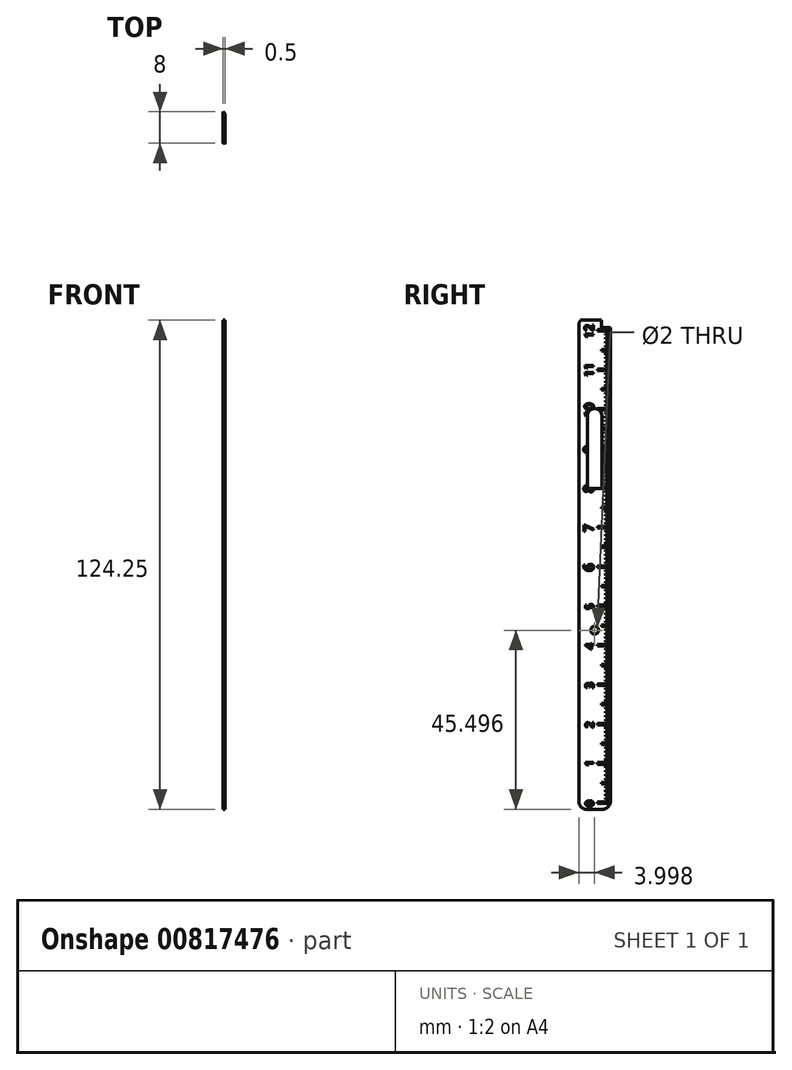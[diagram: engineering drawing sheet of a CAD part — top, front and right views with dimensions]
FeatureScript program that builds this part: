
annotation { "Feature Type Name" : "Feature", "Feature Type Description" : "" }
export const myFeature = defineFeature(function(context is Context, id is Id, definition is map)
    precondition{}
    {
        {
            var Q0;
            Q0=qCreatedBy(makeId("Right.planeOp"),FACE);
            var sketch = newSketch(context, id + "F0", { "sketchPlane" : qUnion([Q0])});
            skLineSegment(sketch, "E0.bottom", {"start": v(-20, 0) * mm, "end": v(-10, 0) * mm});
            skLineSegment(sketch, "E0.top", {"start": v(-20, 160) * mm, "end": v(-10, 160) * mm});
            skLineSegment(sketch, "E0.left", {"start": v(-20, 0) * mm, "end": v(-20, 160) * mm});
            skLineSegment(sketch, "E0.right", {"start": v(-10, 0) * mm, "end": v(-10, 160) * mm});
            skSolve(sketch);
        }
        {
            var Q0;
            Q0=qSketchRegion(id+"F0",true);
            extrude(context, id + "F1", {"entities" : qUnion([Q0]), "depth" : 1 * mm, "offsetDistance" : 25 * mm});
        }
        {
            var Q0;
            Q0=qCreatedBy(makeId("Right.planeOp"),FACE);
            var sketch = newSketch(context, id + "F2", { "sketchPlane" : qUnion([Q0])});
            skLineSegment(sketch, "E1", {"start": v(-12, 0) * mm, "end": v(-12, 150) * mm, "construction": true});
            skLineSegment(sketch, "E2", {"start": v(-14, 0) * mm, "end": v(-14, 150) * mm, "construction": true});
            skLineSegment(sketch, "E3", {"start": v(-13, 0) * mm, "end": v(-13, 150) * mm, "construction": true});
            skLineSegment(sketch, "E4.bottom", {"start": v(-14, 10.4) * mm, "end": v(-10, 10.4) * mm});
            skLineSegment(sketch, "E4.top", {"start": v(-14, 10) * mm, "end": v(-10, 10) * mm});
            skLineSegment(sketch, "E4.left", {"start": v(-14, 10) * mm, "end": v(-14, 10.4) * mm});
            skLineSegment(sketch, "E4.right", {"start": v(-10, 10) * mm, "end": v(-10, 10.4) * mm});
            skLineSegment(sketch, "E5.0.1.0", {"start": v(-14, 20.4) * mm, "end": v(-10, 20.4) * mm});
            skLineSegment(sketch, "E5.0.1.1", {"start": v(-14, 20) * mm, "end": v(-10, 20) * mm});
            skLineSegment(sketch, "E5.0.1.2", {"start": v(-14, 20) * mm, "end": v(-14, 20.4) * mm});
            skLineSegment(sketch, "E5.0.1.3", {"start": v(-10, 20) * mm, "end": v(-10, 20.4) * mm});
            skLineSegment(sketch, "E5.0.2.0", {"start": v(-14, 30.4) * mm, "end": v(-10, 30.4) * mm});
            skLineSegment(sketch, "E5.0.2.1", {"start": v(-14, 30) * mm, "end": v(-10, 30) * mm});
            skLineSegment(sketch, "E5.0.2.2", {"start": v(-14, 30) * mm, "end": v(-14, 30.4) * mm});
            skLineSegment(sketch, "E5.0.2.3", {"start": v(-10, 30) * mm, "end": v(-10, 30.4) * mm});
            skLineSegment(sketch, "E5.0.3.0", {"start": v(-14, 40.4) * mm, "end": v(-10, 40.4) * mm});
            skLineSegment(sketch, "E5.0.3.1", {"start": v(-14, 40) * mm, "end": v(-10, 40) * mm});
            skLineSegment(sketch, "E5.0.3.2", {"start": v(-14, 40) * mm, "end": v(-14, 40.4) * mm});
            skLineSegment(sketch, "E5.0.3.3", {"start": v(-10, 40) * mm, "end": v(-10, 40.4) * mm});
            skLineSegment(sketch, "E5.0.4.0", {"start": v(-14, 50.4) * mm, "end": v(-10, 50.4) * mm});
            skLineSegment(sketch, "E5.0.4.1", {"start": v(-14, 50) * mm, "end": v(-10, 50) * mm});
            skLineSegment(sketch, "E5.0.4.2", {"start": v(-14, 50) * mm, "end": v(-14, 50.4) * mm});
            skLineSegment(sketch, "E5.0.4.3", {"start": v(-10, 50) * mm, "end": v(-10, 50.4) * mm});
            skLineSegment(sketch, "E5.0.5.0", {"start": v(-14, 60.4) * mm, "end": v(-10, 60.4) * mm});
            skLineSegment(sketch, "E5.0.5.1", {"start": v(-14, 60) * mm, "end": v(-10, 60) * mm});
            skLineSegment(sketch, "E5.0.5.2", {"start": v(-14, 60) * mm, "end": v(-14, 60.4) * mm});
            skLineSegment(sketch, "E5.0.5.3", {"start": v(-10, 60) * mm, "end": v(-10, 60.4) * mm});
            skLineSegment(sketch, "E5.0.6.0", {"start": v(-14, 70.4) * mm, "end": v(-10, 70.4) * mm});
            skLineSegment(sketch, "E5.0.6.1", {"start": v(-14, 70) * mm, "end": v(-10, 70) * mm});
            skLineSegment(sketch, "E5.0.6.2", {"start": v(-14, 70) * mm, "end": v(-14, 70.4) * mm});
            skLineSegment(sketch, "E5.0.6.3", {"start": v(-10, 70) * mm, "end": v(-10, 70.4) * mm});
            skLineSegment(sketch, "E5.0.7.0", {"start": v(-14, 80.4) * mm, "end": v(-10, 80.4) * mm});
            skLineSegment(sketch, "E5.0.7.1", {"start": v(-14, 80) * mm, "end": v(-10, 80) * mm});
            skLineSegment(sketch, "E5.0.7.2", {"start": v(-14, 80) * mm, "end": v(-14, 80.4) * mm});
            skLineSegment(sketch, "E5.0.7.3", {"start": v(-10, 80) * mm, "end": v(-10, 80.4) * mm});
            skLineSegment(sketch, "E5.0.8.0", {"start": v(-14, 90.4) * mm, "end": v(-10, 90.4) * mm});
            skLineSegment(sketch, "E5.0.8.1", {"start": v(-14, 90) * mm, "end": v(-10, 90) * mm});
            skLineSegment(sketch, "E5.0.8.2", {"start": v(-14, 90) * mm, "end": v(-14, 90.4) * mm});
            skLineSegment(sketch, "E5.0.8.3", {"start": v(-10, 90) * mm, "end": v(-10, 90.4) * mm});
            skLineSegment(sketch, "E5.0.9.0", {"start": v(-14, 100.4) * mm, "end": v(-10, 100.4) * mm});
            skLineSegment(sketch, "E5.0.9.1", {"start": v(-14, 100) * mm, "end": v(-10, 100) * mm});
            skLineSegment(sketch, "E5.0.9.2", {"start": v(-14, 100) * mm, "end": v(-14, 100.4) * mm});
            skLineSegment(sketch, "E5.0.9.3", {"start": v(-10, 100) * mm, "end": v(-10, 100.4) * mm});
            skLineSegment(sketch, "E5.direction2", {"start": v(-14, 10) * mm, "end": v(-14, 20) * mm, "construction": true});
            skLineSegment(sketch, "E6.0.0.10", {"start": v(-14, 110.4) * mm, "end": v(-10, 110.4) * mm});
            skLineSegment(sketch, "E6.3.0.10", {"start": v(-14, 110) * mm, "end": v(-10, 110) * mm});
            skLineSegment(sketch, "E6.6.0.10", {"start": v(-14, 110) * mm, "end": v(-14, 110.4) * mm});
            skLineSegment(sketch, "E6.9.0.10", {"start": v(-10, 110) * mm, "end": v(-10, 110.4) * mm});
            skLineSegment(sketch, "E6.0.0.11", {"start": v(-14, 120.4) * mm, "end": v(-10, 120.4) * mm});
            skLineSegment(sketch, "E6.3.0.11", {"start": v(-14, 120) * mm, "end": v(-10, 120) * mm});
            skLineSegment(sketch, "E6.6.0.11", {"start": v(-14, 120) * mm, "end": v(-14, 120.4) * mm});
            skLineSegment(sketch, "E6.9.0.11", {"start": v(-10, 120) * mm, "end": v(-10, 120.4) * mm});
            skLineSegment(sketch, "E6.0.0.12", {"start": v(-14, 130.4) * mm, "end": v(-10, 130.4) * mm});
            skLineSegment(sketch, "E6.3.0.12", {"start": v(-14, 130) * mm, "end": v(-10, 130) * mm});
            skLineSegment(sketch, "E6.6.0.12", {"start": v(-14, 130) * mm, "end": v(-14, 130.4) * mm});
            skLineSegment(sketch, "E6.9.0.12", {"start": v(-10, 130) * mm, "end": v(-10, 130.4) * mm});
            skLineSegment(sketch, "E6.0.0.13", {"start": v(-14, 140.4) * mm, "end": v(-10, 140.4) * mm});
            skLineSegment(sketch, "E6.3.0.13", {"start": v(-14, 140) * mm, "end": v(-10, 140) * mm});
            skLineSegment(sketch, "E6.6.0.13", {"start": v(-14, 140) * mm, "end": v(-14, 140.4) * mm});
            skLineSegment(sketch, "E6.9.0.13", {"start": v(-10, 140) * mm, "end": v(-10, 140.4) * mm});
            skLineSegment(sketch, "E7.bottom", {"start": v(-10, 15) * mm, "end": v(-13, 15) * mm});
            skLineSegment(sketch, "E7.top", {"start": v(-10, 15.4) * mm, "end": v(-13, 15.4) * mm});
            skLineSegment(sketch, "E7.left", {"start": v(-10, 15) * mm, "end": v(-10, 15.4) * mm});
            skLineSegment(sketch, "E7.right", {"start": v(-13, 15) * mm, "end": v(-13, 15.4) * mm});
            skLineSegment(sketch, "E8", {"start": v(-22.56, 0) * mm, "end": v(-10, 0) * mm, "construction": true});
            skLineSegment(sketch, "E9", {"start": v(-15, 150) * mm, "end": v(-15, 0) * mm, "construction": true});
            skText(sketch, "E10", { "text": "0", "fontName": "OpenSans-Regular.ttf"});
            skText(sketch, "E11", { "text": "1\n", "fontName": "OpenSans-Regular.ttf"});
            skText(sketch, "E12", { "text": "2", "fontName": "OpenSans-Regular.ttf"});
            skText(sketch, "E13", { "text": "3", "fontName": "OpenSans-Regular.ttf"});
            skText(sketch, "E14", { "text": "4", "fontName": "OpenSans-Regular.ttf"});
            skText(sketch, "E15", { "text": "5", "fontName": "OpenSans-Regular.ttf"});
            skText(sketch, "E16", { "text": "6", "fontName": "OpenSans-Regular.ttf"});
            skText(sketch, "E17", { "text": "7", "fontName": "OpenSans-Regular.ttf"});
            skText(sketch, "E18", { "text": "8", "fontName": "OpenSans-Regular.ttf"});
            skText(sketch, "E19", { "text": "9", "fontName": "OpenSans-Regular.ttf"});
            skText(sketch, "E20", { "text": "10", "fontName": "OpenSans-Regular.ttf"});
            skText(sketch, "E21", { "text": "11", "fontName": "OpenSans-Regular.ttf"});
            skText(sketch, "E22", { "text": "12", "fontName": "OpenSans-Regular.ttf"});
            skText(sketch, "E23", { "text": "13", "fontName": "OpenSans-Regular.ttf"});
            skLineSegment(sketch, "E24.bottom", {"start": v(-12, 11) * mm, "end": v(-10, 11) * mm});
            skLineSegment(sketch, "E24.top", {"start": v(-12, 11.4) * mm, "end": v(-10, 11.4) * mm});
            skLineSegment(sketch, "E24.left", {"start": v(-12, 11) * mm, "end": v(-12, 11.4) * mm});
            skLineSegment(sketch, "E24.right", {"start": v(-10, 11) * mm, "end": v(-10, 11.4) * mm});
            skLineSegment(sketch, "E25.bottom", {"start": v(-12, 12) * mm, "end": v(-10, 12) * mm});
            skLineSegment(sketch, "E25.top", {"start": v(-12, 12.4) * mm, "end": v(-10, 12.4) * mm});
            skLineSegment(sketch, "E25.left", {"start": v(-12, 12) * mm, "end": v(-12, 12.4) * mm});
            skLineSegment(sketch, "E25.right", {"start": v(-10, 12) * mm, "end": v(-10, 12.4) * mm});
            skLineSegment(sketch, "E26.bottom", {"start": v(-12, 13) * mm, "end": v(-10, 13) * mm});
            skLineSegment(sketch, "E26.top", {"start": v(-12, 13.4) * mm, "end": v(-10, 13.4) * mm});
            skLineSegment(sketch, "E26.left", {"start": v(-12, 13) * mm, "end": v(-12, 13.4) * mm});
            skLineSegment(sketch, "E26.right", {"start": v(-10, 13) * mm, "end": v(-10, 13.4) * mm});
            skLineSegment(sketch, "E27.bottom", {"start": v(-12, 14) * mm, "end": v(-10, 14) * mm});
            skLineSegment(sketch, "E27.top", {"start": v(-12, 14.4) * mm, "end": v(-10, 14.4) * mm});
            skLineSegment(sketch, "E27.left", {"start": v(-12, 14) * mm, "end": v(-12, 14.4) * mm});
            skLineSegment(sketch, "E27.right", {"start": v(-10, 14) * mm, "end": v(-10, 14.4) * mm});
            skLineSegment(sketch, "E28.bottom", {"start": v(-12, 16) * mm, "end": v(-10, 16) * mm});
            skLineSegment(sketch, "E28.top", {"start": v(-12, 16.4) * mm, "end": v(-10, 16.4) * mm});
            skLineSegment(sketch, "E28.left", {"start": v(-12, 16) * mm, "end": v(-12, 16.4) * mm});
            skLineSegment(sketch, "E28.right", {"start": v(-10, 16) * mm, "end": v(-10, 16.4) * mm});
            skLineSegment(sketch, "E29.bottom", {"start": v(-12, 17) * mm, "end": v(-10, 17) * mm});
            skLineSegment(sketch, "E29.top", {"start": v(-12, 17.4) * mm, "end": v(-10, 17.4) * mm});
            skLineSegment(sketch, "E29.left", {"start": v(-12, 17) * mm, "end": v(-12, 17.4) * mm});
            skLineSegment(sketch, "E29.right", {"start": v(-10, 17) * mm, "end": v(-10, 17.4) * mm});
            skLineSegment(sketch, "E30.bottom", {"start": v(-12, 18) * mm, "end": v(-10, 18) * mm});
            skLineSegment(sketch, "E30.top", {"start": v(-12, 18.4) * mm, "end": v(-10, 18.4) * mm});
            skLineSegment(sketch, "E30.left", {"start": v(-12, 18) * mm, "end": v(-12, 18.4) * mm});
            skLineSegment(sketch, "E30.right", {"start": v(-10, 18) * mm, "end": v(-10, 18.4) * mm});
            skLineSegment(sketch, "E31.bottom", {"start": v(-12, 19) * mm, "end": v(-10, 19) * mm});
            skLineSegment(sketch, "E31.top", {"start": v(-12, 19.4) * mm, "end": v(-10, 19.4) * mm});
            skLineSegment(sketch, "E31.left", {"start": v(-12, 19) * mm, "end": v(-12, 19.4) * mm});
            skLineSegment(sketch, "E31.right", {"start": v(-10, 19) * mm, "end": v(-10, 19.4) * mm});
            skLineSegment(sketch, "E32.0.1.0", {"start": v(-12, 22) * mm, "end": v(-10, 22) * mm});
            skLineSegment(sketch, "E32.0.1.1", {"start": v(-12, 21.4) * mm, "end": v(-10, 21.4) * mm});
            skLineSegment(sketch, "E32.0.1.2", {"start": v(-12, 23.4) * mm, "end": v(-10, 23.4) * mm});
            skLineSegment(sketch, "E32.0.1.3", {"start": v(-12, 28.4) * mm, "end": v(-10, 28.4) * mm});
            skLineSegment(sketch, "E32.0.1.4", {"start": v(-12, 22.4) * mm, "end": v(-10, 22.4) * mm});
            skLineSegment(sketch, "E32.0.1.5", {"start": v(-12, 23) * mm, "end": v(-10, 23) * mm});
            skLineSegment(sketch, "E32.0.1.6", {"start": v(-10, 25.4) * mm, "end": v(-13, 25.4) * mm});
            skLineSegment(sketch, "E32.0.1.7", {"start": v(-12, 29) * mm, "end": v(-10, 29) * mm});
            skLineSegment(sketch, "E32.0.1.8", {"start": v(-12, 29.4) * mm, "end": v(-10, 29.4) * mm});
            skLineSegment(sketch, "E32.0.1.9", {"start": v(-12, 24.4) * mm, "end": v(-10, 24.4) * mm});
            skLineSegment(sketch, "E32.0.1.10", {"start": v(-12, 28) * mm, "end": v(-10, 28) * mm});
            skLineSegment(sketch, "E32.0.1.11", {"start": v(-12, 26) * mm, "end": v(-10, 26) * mm});
            skLineSegment(sketch, "E32.0.1.12", {"start": v(-12, 27) * mm, "end": v(-10, 27) * mm});
            skLineSegment(sketch, "E32.0.1.13", {"start": v(-12, 26.4) * mm, "end": v(-10, 26.4) * mm});
            skLineSegment(sketch, "E32.0.1.14", {"start": v(-12, 21) * mm, "end": v(-10, 21) * mm});
            skLineSegment(sketch, "E32.0.1.15", {"start": v(-10, 25) * mm, "end": v(-13, 25) * mm});
            skLineSegment(sketch, "E32.0.1.16", {"start": v(-12, 10) * mm, "end": v(-12, 160) * mm, "construction": true});
            skLineSegment(sketch, "E32.0.1.17", {"start": v(-13, 10) * mm, "end": v(-13, 160) * mm, "construction": true});
            skLineSegment(sketch, "E32.0.1.18", {"start": v(-12, 24) * mm, "end": v(-10, 24) * mm});
            skLineSegment(sketch, "E32.0.1.19", {"start": v(-12, 27.4) * mm, "end": v(-10, 27.4) * mm});
            skLineSegment(sketch, "E32.0.1.20", {"start": v(-12, 21) * mm, "end": v(-12, 21.4) * mm});
            skLineSegment(sketch, "E32.0.1.21", {"start": v(-10, 24) * mm, "end": v(-10, 24.4) * mm});
            skLineSegment(sketch, "E32.0.1.22", {"start": v(-10, 27) * mm, "end": v(-10, 27.4) * mm});
            skLineSegment(sketch, "E32.0.1.23", {"start": v(-12, 29) * mm, "end": v(-12, 29.4) * mm});
            skLineSegment(sketch, "E32.0.1.24", {"start": v(-10, 25) * mm, "end": v(-10, 25.4) * mm});
            skLineSegment(sketch, "E32.0.1.25", {"start": v(-12, 24) * mm, "end": v(-12, 24.4) * mm});
            skLineSegment(sketch, "E32.0.1.26", {"start": v(-12, 26) * mm, "end": v(-12, 26.4) * mm});
            skLineSegment(sketch, "E32.0.1.27", {"start": v(-10, 28) * mm, "end": v(-10, 28.4) * mm});
            skLineSegment(sketch, "E32.0.1.28", {"start": v(-12, 28) * mm, "end": v(-12, 28.4) * mm});
            skLineSegment(sketch, "E32.0.1.29", {"start": v(-10, 21) * mm, "end": v(-10, 21.4) * mm});
            skLineSegment(sketch, "E32.0.1.30", {"start": v(-10, 26) * mm, "end": v(-10, 26.4) * mm});
            skLineSegment(sketch, "E32.0.1.31", {"start": v(-10, 29) * mm, "end": v(-10, 29.4) * mm});
            skLineSegment(sketch, "E32.0.1.32", {"start": v(-12, 22) * mm, "end": v(-12, 22.4) * mm});
            skLineSegment(sketch, "E32.0.1.33", {"start": v(-10, 23) * mm, "end": v(-10, 23.4) * mm});
            skLineSegment(sketch, "E32.0.1.34", {"start": v(-13, 25) * mm, "end": v(-13, 25.4) * mm});
            skLineSegment(sketch, "E32.0.1.35", {"start": v(-10, 22) * mm, "end": v(-10, 22.4) * mm});
            skLineSegment(sketch, "E32.0.1.36", {"start": v(-12, 27) * mm, "end": v(-12, 27.4) * mm});
            skLineSegment(sketch, "E32.0.1.37", {"start": v(-12, 23) * mm, "end": v(-12, 23.4) * mm});
            skLineSegment(sketch, "E32.0.2.0", {"start": v(-12, 32) * mm, "end": v(-10, 32) * mm});
            skLineSegment(sketch, "E32.0.2.1", {"start": v(-12, 31.4) * mm, "end": v(-10, 31.4) * mm});
            skLineSegment(sketch, "E32.0.2.2", {"start": v(-12, 33.4) * mm, "end": v(-10, 33.4) * mm});
            skLineSegment(sketch, "E32.0.2.3", {"start": v(-12, 38.4) * mm, "end": v(-10, 38.4) * mm});
            skLineSegment(sketch, "E32.0.2.4", {"start": v(-12, 32.4) * mm, "end": v(-10, 32.4) * mm});
            skLineSegment(sketch, "E32.0.2.5", {"start": v(-12, 33) * mm, "end": v(-10, 33) * mm});
            skLineSegment(sketch, "E32.0.2.6", {"start": v(-10, 35.4) * mm, "end": v(-13, 35.4) * mm});
            skLineSegment(sketch, "E32.0.2.7", {"start": v(-12, 39) * mm, "end": v(-10, 39) * mm});
            skLineSegment(sketch, "E32.0.2.8", {"start": v(-12, 39.4) * mm, "end": v(-10, 39.4) * mm});
            skLineSegment(sketch, "E32.0.2.9", {"start": v(-12, 34.4) * mm, "end": v(-10, 34.4) * mm});
            skLineSegment(sketch, "E32.0.2.10", {"start": v(-12, 38) * mm, "end": v(-10, 38) * mm});
            skLineSegment(sketch, "E32.0.2.11", {"start": v(-12, 36) * mm, "end": v(-10, 36) * mm});
            skLineSegment(sketch, "E32.0.2.12", {"start": v(-12, 37) * mm, "end": v(-10, 37) * mm});
            skLineSegment(sketch, "E32.0.2.13", {"start": v(-12, 36.4) * mm, "end": v(-10, 36.4) * mm});
            skLineSegment(sketch, "E32.0.2.14", {"start": v(-12, 31) * mm, "end": v(-10, 31) * mm});
            skLineSegment(sketch, "E32.0.2.15", {"start": v(-10, 35) * mm, "end": v(-13, 35) * mm});
            skLineSegment(sketch, "E32.0.2.16", {"start": v(-12, 20) * mm, "end": v(-12, 170) * mm, "construction": true});
            skLineSegment(sketch, "E32.0.2.17", {"start": v(-13, 20) * mm, "end": v(-13, 170) * mm, "construction": true});
            skLineSegment(sketch, "E32.0.2.18", {"start": v(-12, 34) * mm, "end": v(-10, 34) * mm});
            skLineSegment(sketch, "E32.0.2.19", {"start": v(-12, 37.4) * mm, "end": v(-10, 37.4) * mm});
            skLineSegment(sketch, "E32.0.2.20", {"start": v(-12, 31) * mm, "end": v(-12, 31.4) * mm});
            skLineSegment(sketch, "E32.0.2.21", {"start": v(-10, 34) * mm, "end": v(-10, 34.4) * mm});
            skLineSegment(sketch, "E32.0.2.22", {"start": v(-10, 37) * mm, "end": v(-10, 37.4) * mm});
            skLineSegment(sketch, "E32.0.2.23", {"start": v(-12, 39) * mm, "end": v(-12, 39.4) * mm});
            skLineSegment(sketch, "E32.0.2.24", {"start": v(-10, 35) * mm, "end": v(-10, 35.4) * mm});
            skLineSegment(sketch, "E32.0.2.25", {"start": v(-12, 34) * mm, "end": v(-12, 34.4) * mm});
            skLineSegment(sketch, "E32.0.2.26", {"start": v(-12, 36) * mm, "end": v(-12, 36.4) * mm});
            skLineSegment(sketch, "E32.0.2.27", {"start": v(-10, 38) * mm, "end": v(-10, 38.4) * mm});
            skLineSegment(sketch, "E32.0.2.28", {"start": v(-12, 38) * mm, "end": v(-12, 38.4) * mm});
            skLineSegment(sketch, "E32.0.2.29", {"start": v(-10, 31) * mm, "end": v(-10, 31.4) * mm});
            skLineSegment(sketch, "E32.0.2.30", {"start": v(-10, 36) * mm, "end": v(-10, 36.4) * mm});
            skLineSegment(sketch, "E32.0.2.31", {"start": v(-10, 39) * mm, "end": v(-10, 39.4) * mm});
            skLineSegment(sketch, "E32.0.2.32", {"start": v(-12, 32) * mm, "end": v(-12, 32.4) * mm});
            skLineSegment(sketch, "E32.0.2.33", {"start": v(-10, 33) * mm, "end": v(-10, 33.4) * mm});
            skLineSegment(sketch, "E32.0.2.34", {"start": v(-13, 35) * mm, "end": v(-13, 35.4) * mm});
            skLineSegment(sketch, "E32.0.2.35", {"start": v(-10, 32) * mm, "end": v(-10, 32.4) * mm});
            skLineSegment(sketch, "E32.0.2.36", {"start": v(-12, 37) * mm, "end": v(-12, 37.4) * mm});
            skLineSegment(sketch, "E32.0.2.37", {"start": v(-12, 33) * mm, "end": v(-12, 33.4) * mm});
            skLineSegment(sketch, "E32.0.3.0", {"start": v(-12, 42) * mm, "end": v(-10, 42) * mm});
            skLineSegment(sketch, "E32.0.3.1", {"start": v(-12, 41.4) * mm, "end": v(-10, 41.4) * mm});
            skLineSegment(sketch, "E32.0.3.2", {"start": v(-12, 43.4) * mm, "end": v(-10, 43.4) * mm});
            skLineSegment(sketch, "E32.0.3.3", {"start": v(-12, 48.4) * mm, "end": v(-10, 48.4) * mm});
            skLineSegment(sketch, "E32.0.3.4", {"start": v(-12, 42.4) * mm, "end": v(-10, 42.4) * mm});
            skLineSegment(sketch, "E32.0.3.5", {"start": v(-12, 43) * mm, "end": v(-10, 43) * mm});
            skLineSegment(sketch, "E32.0.3.6", {"start": v(-10, 45.4) * mm, "end": v(-13, 45.4) * mm});
            skLineSegment(sketch, "E32.0.3.7", {"start": v(-12, 49) * mm, "end": v(-10, 49) * mm});
            skLineSegment(sketch, "E32.0.3.8", {"start": v(-12, 49.4) * mm, "end": v(-10, 49.4) * mm});
            skLineSegment(sketch, "E32.0.3.9", {"start": v(-12, 44.4) * mm, "end": v(-10, 44.4) * mm});
            skLineSegment(sketch, "E32.0.3.10", {"start": v(-12, 48) * mm, "end": v(-10, 48) * mm});
            skLineSegment(sketch, "E32.0.3.11", {"start": v(-12, 46) * mm, "end": v(-10, 46) * mm});
            skLineSegment(sketch, "E32.0.3.12", {"start": v(-12, 47) * mm, "end": v(-10, 47) * mm});
            skLineSegment(sketch, "E32.0.3.13", {"start": v(-12, 46.4) * mm, "end": v(-10, 46.4) * mm});
            skLineSegment(sketch, "E32.0.3.14", {"start": v(-12, 41) * mm, "end": v(-10, 41) * mm});
            skLineSegment(sketch, "E32.0.3.15", {"start": v(-10, 45) * mm, "end": v(-13, 45) * mm});
            skLineSegment(sketch, "E32.0.3.16", {"start": v(-12, 30) * mm, "end": v(-12, 180) * mm, "construction": true});
            skLineSegment(sketch, "E32.0.3.17", {"start": v(-13, 30) * mm, "end": v(-13, 180) * mm, "construction": true});
            skLineSegment(sketch, "E32.0.3.18", {"start": v(-12, 44) * mm, "end": v(-10, 44) * mm});
            skLineSegment(sketch, "E32.0.3.19", {"start": v(-12, 47.4) * mm, "end": v(-10, 47.4) * mm});
            skLineSegment(sketch, "E32.0.3.20", {"start": v(-12, 41) * mm, "end": v(-12, 41.4) * mm});
            skLineSegment(sketch, "E32.0.3.21", {"start": v(-10, 44) * mm, "end": v(-10, 44.4) * mm});
            skLineSegment(sketch, "E32.0.3.22", {"start": v(-10, 47) * mm, "end": v(-10, 47.4) * mm});
            skLineSegment(sketch, "E32.0.3.23", {"start": v(-12, 49) * mm, "end": v(-12, 49.4) * mm});
            skLineSegment(sketch, "E32.0.3.24", {"start": v(-10, 45) * mm, "end": v(-10, 45.4) * mm});
            skLineSegment(sketch, "E32.0.3.25", {"start": v(-12, 44) * mm, "end": v(-12, 44.4) * mm});
            skLineSegment(sketch, "E32.0.3.26", {"start": v(-12, 46) * mm, "end": v(-12, 46.4) * mm});
            skLineSegment(sketch, "E32.0.3.27", {"start": v(-10, 48) * mm, "end": v(-10, 48.4) * mm});
            skLineSegment(sketch, "E32.0.3.28", {"start": v(-12, 48) * mm, "end": v(-12, 48.4) * mm});
            skLineSegment(sketch, "E32.0.3.29", {"start": v(-10, 41) * mm, "end": v(-10, 41.4) * mm});
            skLineSegment(sketch, "E32.0.3.30", {"start": v(-10, 46) * mm, "end": v(-10, 46.4) * mm});
            skLineSegment(sketch, "E32.0.3.31", {"start": v(-10, 49) * mm, "end": v(-10, 49.4) * mm});
            skLineSegment(sketch, "E32.0.3.32", {"start": v(-12, 42) * mm, "end": v(-12, 42.4) * mm});
            skLineSegment(sketch, "E32.0.3.33", {"start": v(-10, 43) * mm, "end": v(-10, 43.4) * mm});
            skLineSegment(sketch, "E32.0.3.34", {"start": v(-13, 45) * mm, "end": v(-13, 45.4) * mm});
            skLineSegment(sketch, "E32.0.3.35", {"start": v(-10, 42) * mm, "end": v(-10, 42.4) * mm});
            skLineSegment(sketch, "E32.0.3.36", {"start": v(-12, 47) * mm, "end": v(-12, 47.4) * mm});
            skLineSegment(sketch, "E32.0.3.37", {"start": v(-12, 43) * mm, "end": v(-12, 43.4) * mm});
            skLineSegment(sketch, "E32.0.4.0", {"start": v(-12, 52) * mm, "end": v(-10, 52) * mm});
            skLineSegment(sketch, "E32.0.4.1", {"start": v(-12, 51.4) * mm, "end": v(-10, 51.4) * mm});
            skLineSegment(sketch, "E32.0.4.2", {"start": v(-12, 53.4) * mm, "end": v(-10, 53.4) * mm});
            skLineSegment(sketch, "E32.0.4.3", {"start": v(-12, 58.4) * mm, "end": v(-10, 58.4) * mm});
            skLineSegment(sketch, "E32.0.4.4", {"start": v(-12, 52.4) * mm, "end": v(-10, 52.4) * mm});
            skLineSegment(sketch, "E32.0.4.5", {"start": v(-12, 53) * mm, "end": v(-10, 53) * mm});
            skLineSegment(sketch, "E32.0.4.6", {"start": v(-10, 55.4) * mm, "end": v(-13, 55.4) * mm});
            skLineSegment(sketch, "E32.0.4.7", {"start": v(-12, 59) * mm, "end": v(-10, 59) * mm});
            skLineSegment(sketch, "E32.0.4.8", {"start": v(-12, 59.4) * mm, "end": v(-10, 59.4) * mm});
            skLineSegment(sketch, "E32.0.4.9", {"start": v(-12, 54.4) * mm, "end": v(-10, 54.4) * mm});
            skLineSegment(sketch, "E32.0.4.10", {"start": v(-12, 58) * mm, "end": v(-10, 58) * mm});
            skLineSegment(sketch, "E32.0.4.11", {"start": v(-12, 56) * mm, "end": v(-10, 56) * mm});
            skLineSegment(sketch, "E32.0.4.12", {"start": v(-12, 57) * mm, "end": v(-10, 57) * mm});
            skLineSegment(sketch, "E32.0.4.13", {"start": v(-12, 56.4) * mm, "end": v(-10, 56.4) * mm});
            skLineSegment(sketch, "E32.0.4.14", {"start": v(-12, 51) * mm, "end": v(-10, 51) * mm});
            skLineSegment(sketch, "E32.0.4.15", {"start": v(-10, 55) * mm, "end": v(-13, 55) * mm});
            skLineSegment(sketch, "E32.0.4.16", {"start": v(-12, 40) * mm, "end": v(-12, 190) * mm, "construction": true});
            skLineSegment(sketch, "E32.0.4.17", {"start": v(-13, 40) * mm, "end": v(-13, 190) * mm, "construction": true});
            skLineSegment(sketch, "E32.0.4.18", {"start": v(-12, 54) * mm, "end": v(-10, 54) * mm});
            skLineSegment(sketch, "E32.0.4.19", {"start": v(-12, 57.4) * mm, "end": v(-10, 57.4) * mm});
            skLineSegment(sketch, "E32.0.4.20", {"start": v(-12, 51) * mm, "end": v(-12, 51.4) * mm});
            skLineSegment(sketch, "E32.0.4.21", {"start": v(-10, 54) * mm, "end": v(-10, 54.4) * mm});
            skLineSegment(sketch, "E32.0.4.22", {"start": v(-10, 57) * mm, "end": v(-10, 57.4) * mm});
            skLineSegment(sketch, "E32.0.4.23", {"start": v(-12, 59) * mm, "end": v(-12, 59.4) * mm});
            skLineSegment(sketch, "E32.0.4.24", {"start": v(-10, 55) * mm, "end": v(-10, 55.4) * mm});
            skLineSegment(sketch, "E32.0.4.25", {"start": v(-12, 54) * mm, "end": v(-12, 54.4) * mm});
            skLineSegment(sketch, "E32.0.4.26", {"start": v(-12, 56) * mm, "end": v(-12, 56.4) * mm});
            skLineSegment(sketch, "E32.0.4.27", {"start": v(-10, 58) * mm, "end": v(-10, 58.4) * mm});
            skLineSegment(sketch, "E32.0.4.28", {"start": v(-12, 58) * mm, "end": v(-12, 58.4) * mm});
            skLineSegment(sketch, "E32.0.4.29", {"start": v(-10, 51) * mm, "end": v(-10, 51.4) * mm});
            skLineSegment(sketch, "E32.0.4.30", {"start": v(-10, 56) * mm, "end": v(-10, 56.4) * mm});
            skLineSegment(sketch, "E32.0.4.31", {"start": v(-10, 59) * mm, "end": v(-10, 59.4) * mm});
            skLineSegment(sketch, "E32.0.4.32", {"start": v(-12, 52) * mm, "end": v(-12, 52.4) * mm});
            skLineSegment(sketch, "E32.0.4.33", {"start": v(-10, 53) * mm, "end": v(-10, 53.4) * mm});
            skLineSegment(sketch, "E32.0.4.34", {"start": v(-13, 55) * mm, "end": v(-13, 55.4) * mm});
            skLineSegment(sketch, "E32.0.4.35", {"start": v(-10, 52) * mm, "end": v(-10, 52.4) * mm});
            skLineSegment(sketch, "E32.0.4.36", {"start": v(-12, 57) * mm, "end": v(-12, 57.4) * mm});
            skLineSegment(sketch, "E32.0.4.37", {"start": v(-12, 53) * mm, "end": v(-12, 53.4) * mm});
            skLineSegment(sketch, "E32.0.5.0", {"start": v(-12, 62) * mm, "end": v(-10, 62) * mm});
            skLineSegment(sketch, "E32.0.5.1", {"start": v(-12, 61.4) * mm, "end": v(-10, 61.4) * mm});
            skLineSegment(sketch, "E32.0.5.2", {"start": v(-12, 63.4) * mm, "end": v(-10, 63.4) * mm});
            skLineSegment(sketch, "E32.0.5.3", {"start": v(-12, 68.4) * mm, "end": v(-10, 68.4) * mm});
            skLineSegment(sketch, "E32.0.5.4", {"start": v(-12, 62.4) * mm, "end": v(-10, 62.4) * mm});
            skLineSegment(sketch, "E32.0.5.5", {"start": v(-12, 63) * mm, "end": v(-10, 63) * mm});
            skLineSegment(sketch, "E32.0.5.6", {"start": v(-10, 65.4) * mm, "end": v(-13, 65.4) * mm});
            skLineSegment(sketch, "E32.0.5.7", {"start": v(-12, 69) * mm, "end": v(-10, 69) * mm});
            skLineSegment(sketch, "E32.0.5.8", {"start": v(-12, 69.4) * mm, "end": v(-10, 69.4) * mm});
            skLineSegment(sketch, "E32.0.5.9", {"start": v(-12, 64.4) * mm, "end": v(-10, 64.4) * mm});
            skLineSegment(sketch, "E32.0.5.10", {"start": v(-12, 68) * mm, "end": v(-10, 68) * mm});
            skLineSegment(sketch, "E32.0.5.11", {"start": v(-12, 66) * mm, "end": v(-10, 66) * mm});
            skLineSegment(sketch, "E32.0.5.12", {"start": v(-12, 67) * mm, "end": v(-10, 67) * mm});
            skLineSegment(sketch, "E32.0.5.13", {"start": v(-12, 66.4) * mm, "end": v(-10, 66.4) * mm});
            skLineSegment(sketch, "E32.0.5.14", {"start": v(-12, 61) * mm, "end": v(-10, 61) * mm});
            skLineSegment(sketch, "E32.0.5.15", {"start": v(-10, 65) * mm, "end": v(-13, 65) * mm});
            skLineSegment(sketch, "E32.0.5.16", {"start": v(-12, 50) * mm, "end": v(-12, 200) * mm, "construction": true});
            skLineSegment(sketch, "E32.0.5.17", {"start": v(-13, 50) * mm, "end": v(-13, 200) * mm, "construction": true});
            skLineSegment(sketch, "E32.0.5.18", {"start": v(-12, 64) * mm, "end": v(-10, 64) * mm});
            skLineSegment(sketch, "E32.0.5.19", {"start": v(-12, 67.4) * mm, "end": v(-10, 67.4) * mm});
            skLineSegment(sketch, "E32.0.5.20", {"start": v(-12, 61) * mm, "end": v(-12, 61.4) * mm});
            skLineSegment(sketch, "E32.0.5.21", {"start": v(-10, 64) * mm, "end": v(-10, 64.4) * mm});
            skLineSegment(sketch, "E32.0.5.22", {"start": v(-10, 67) * mm, "end": v(-10, 67.4) * mm});
            skLineSegment(sketch, "E32.0.5.23", {"start": v(-12, 69) * mm, "end": v(-12, 69.4) * mm});
            skLineSegment(sketch, "E32.0.5.24", {"start": v(-10, 65) * mm, "end": v(-10, 65.4) * mm});
            skLineSegment(sketch, "E32.0.5.25", {"start": v(-12, 64) * mm, "end": v(-12, 64.4) * mm});
            skLineSegment(sketch, "E32.0.5.26", {"start": v(-12, 66) * mm, "end": v(-12, 66.4) * mm});
            skLineSegment(sketch, "E32.0.5.27", {"start": v(-10, 68) * mm, "end": v(-10, 68.4) * mm});
            skLineSegment(sketch, "E32.0.5.28", {"start": v(-12, 68) * mm, "end": v(-12, 68.4) * mm});
            skLineSegment(sketch, "E32.0.5.29", {"start": v(-10, 61) * mm, "end": v(-10, 61.4) * mm});
            skLineSegment(sketch, "E32.0.5.30", {"start": v(-10, 66) * mm, "end": v(-10, 66.4) * mm});
            skLineSegment(sketch, "E32.0.5.31", {"start": v(-10, 69) * mm, "end": v(-10, 69.4) * mm});
            skLineSegment(sketch, "E32.0.5.32", {"start": v(-12, 62) * mm, "end": v(-12, 62.4) * mm});
            skLineSegment(sketch, "E32.0.5.33", {"start": v(-10, 63) * mm, "end": v(-10, 63.4) * mm});
            skLineSegment(sketch, "E32.0.5.34", {"start": v(-13, 65) * mm, "end": v(-13, 65.4) * mm});
            skLineSegment(sketch, "E32.0.5.35", {"start": v(-10, 62) * mm, "end": v(-10, 62.4) * mm});
            skLineSegment(sketch, "E32.0.5.36", {"start": v(-12, 67) * mm, "end": v(-12, 67.4) * mm});
            skLineSegment(sketch, "E32.0.5.37", {"start": v(-12, 63) * mm, "end": v(-12, 63.4) * mm});
            skLineSegment(sketch, "E32.0.6.0", {"start": v(-12, 72) * mm, "end": v(-10, 72) * mm});
            skLineSegment(sketch, "E32.0.6.1", {"start": v(-12, 71.4) * mm, "end": v(-10, 71.4) * mm});
            skLineSegment(sketch, "E32.0.6.2", {"start": v(-12, 73.4) * mm, "end": v(-10, 73.4) * mm});
            skLineSegment(sketch, "E32.0.6.3", {"start": v(-12, 78.4) * mm, "end": v(-10, 78.4) * mm});
            skLineSegment(sketch, "E32.0.6.4", {"start": v(-12, 72.4) * mm, "end": v(-10, 72.4) * mm});
            skLineSegment(sketch, "E32.0.6.5", {"start": v(-12, 73) * mm, "end": v(-10, 73) * mm});
            skLineSegment(sketch, "E32.0.6.6", {"start": v(-10, 75.4) * mm, "end": v(-13, 75.4) * mm});
            skLineSegment(sketch, "E32.0.6.7", {"start": v(-12, 79) * mm, "end": v(-10, 79) * mm});
            skLineSegment(sketch, "E32.0.6.8", {"start": v(-12, 79.4) * mm, "end": v(-10, 79.4) * mm});
            skLineSegment(sketch, "E32.0.6.9", {"start": v(-12, 74.4) * mm, "end": v(-10, 74.4) * mm});
            skLineSegment(sketch, "E32.0.6.10", {"start": v(-12, 78) * mm, "end": v(-10, 78) * mm});
            skLineSegment(sketch, "E32.0.6.11", {"start": v(-12, 76) * mm, "end": v(-10, 76) * mm});
            skLineSegment(sketch, "E32.0.6.12", {"start": v(-12, 77) * mm, "end": v(-10, 77) * mm});
            skLineSegment(sketch, "E32.0.6.13", {"start": v(-12, 76.4) * mm, "end": v(-10, 76.4) * mm});
            skLineSegment(sketch, "E32.0.6.14", {"start": v(-12, 71) * mm, "end": v(-10, 71) * mm});
            skLineSegment(sketch, "E32.0.6.15", {"start": v(-10, 75) * mm, "end": v(-13, 75) * mm});
            skLineSegment(sketch, "E32.0.6.16", {"start": v(-12, 60) * mm, "end": v(-12, 210) * mm, "construction": true});
            skLineSegment(sketch, "E32.0.6.17", {"start": v(-13, 60) * mm, "end": v(-13, 210) * mm, "construction": true});
            skLineSegment(sketch, "E32.0.6.18", {"start": v(-12, 74) * mm, "end": v(-10, 74) * mm});
            skLineSegment(sketch, "E32.0.6.19", {"start": v(-12, 77.4) * mm, "end": v(-10, 77.4) * mm});
            skLineSegment(sketch, "E32.0.6.20", {"start": v(-12, 71) * mm, "end": v(-12, 71.4) * mm});
            skLineSegment(sketch, "E32.0.6.21", {"start": v(-10, 74) * mm, "end": v(-10, 74.4) * mm});
            skLineSegment(sketch, "E32.0.6.22", {"start": v(-10, 77) * mm, "end": v(-10, 77.4) * mm});
            skLineSegment(sketch, "E32.0.6.23", {"start": v(-12, 79) * mm, "end": v(-12, 79.4) * mm});
            skLineSegment(sketch, "E32.0.6.24", {"start": v(-10, 75) * mm, "end": v(-10, 75.4) * mm});
            skLineSegment(sketch, "E32.0.6.25", {"start": v(-12, 74) * mm, "end": v(-12, 74.4) * mm});
            skLineSegment(sketch, "E32.0.6.26", {"start": v(-12, 76) * mm, "end": v(-12, 76.4) * mm});
            skLineSegment(sketch, "E32.0.6.27", {"start": v(-10, 78) * mm, "end": v(-10, 78.4) * mm});
            skLineSegment(sketch, "E32.0.6.28", {"start": v(-12, 78) * mm, "end": v(-12, 78.4) * mm});
            skLineSegment(sketch, "E32.0.6.29", {"start": v(-10, 71) * mm, "end": v(-10, 71.4) * mm});
            skLineSegment(sketch, "E32.0.6.30", {"start": v(-10, 76) * mm, "end": v(-10, 76.4) * mm});
            skLineSegment(sketch, "E32.0.6.31", {"start": v(-10, 79) * mm, "end": v(-10, 79.4) * mm});
            skLineSegment(sketch, "E32.0.6.32", {"start": v(-12, 72) * mm, "end": v(-12, 72.4) * mm});
            skLineSegment(sketch, "E32.0.6.33", {"start": v(-10, 73) * mm, "end": v(-10, 73.4) * mm});
            skLineSegment(sketch, "E32.0.6.34", {"start": v(-13, 75) * mm, "end": v(-13, 75.4) * mm});
            skLineSegment(sketch, "E32.0.6.35", {"start": v(-10, 72) * mm, "end": v(-10, 72.4) * mm});
            skLineSegment(sketch, "E32.0.6.36", {"start": v(-12, 77) * mm, "end": v(-12, 77.4) * mm});
            skLineSegment(sketch, "E32.0.6.37", {"start": v(-12, 73) * mm, "end": v(-12, 73.4) * mm});
            skLineSegment(sketch, "E32.0.7.0", {"start": v(-12, 82) * mm, "end": v(-10, 82) * mm});
            skLineSegment(sketch, "E32.0.7.1", {"start": v(-12, 81.4) * mm, "end": v(-10, 81.4) * mm});
            skLineSegment(sketch, "E32.0.7.2", {"start": v(-12, 83.4) * mm, "end": v(-10, 83.4) * mm});
            skLineSegment(sketch, "E32.0.7.3", {"start": v(-12, 88.4) * mm, "end": v(-10, 88.4) * mm});
            skLineSegment(sketch, "E32.0.7.4", {"start": v(-12, 82.4) * mm, "end": v(-10, 82.4) * mm});
            skLineSegment(sketch, "E32.0.7.5", {"start": v(-12, 83) * mm, "end": v(-10, 83) * mm});
            skLineSegment(sketch, "E32.0.7.6", {"start": v(-10, 85.4) * mm, "end": v(-13, 85.4) * mm});
            skLineSegment(sketch, "E32.0.7.7", {"start": v(-12, 89) * mm, "end": v(-10, 89) * mm});
            skLineSegment(sketch, "E32.0.7.8", {"start": v(-12, 89.4) * mm, "end": v(-10, 89.4) * mm});
            skLineSegment(sketch, "E32.0.7.9", {"start": v(-12, 84.4) * mm, "end": v(-10, 84.4) * mm});
            skLineSegment(sketch, "E32.0.7.10", {"start": v(-12, 88) * mm, "end": v(-10, 88) * mm});
            skLineSegment(sketch, "E32.0.7.11", {"start": v(-12, 86) * mm, "end": v(-10, 86) * mm});
            skLineSegment(sketch, "E32.0.7.12", {"start": v(-12, 87) * mm, "end": v(-10, 87) * mm});
            skLineSegment(sketch, "E32.0.7.13", {"start": v(-12, 86.4) * mm, "end": v(-10, 86.4) * mm});
            skLineSegment(sketch, "E32.0.7.14", {"start": v(-12, 81) * mm, "end": v(-10, 81) * mm});
            skLineSegment(sketch, "E32.0.7.15", {"start": v(-10, 85) * mm, "end": v(-13, 85) * mm});
            skLineSegment(sketch, "E32.0.7.16", {"start": v(-12, 70) * mm, "end": v(-12, 220) * mm, "construction": true});
            skLineSegment(sketch, "E32.0.7.17", {"start": v(-13, 70) * mm, "end": v(-13, 220) * mm, "construction": true});
            skLineSegment(sketch, "E32.0.7.18", {"start": v(-12, 84) * mm, "end": v(-10, 84) * mm});
            skLineSegment(sketch, "E32.0.7.19", {"start": v(-12, 87.4) * mm, "end": v(-10, 87.4) * mm});
            skLineSegment(sketch, "E32.0.7.20", {"start": v(-12, 81) * mm, "end": v(-12, 81.4) * mm});
            skLineSegment(sketch, "E32.0.7.21", {"start": v(-10, 84) * mm, "end": v(-10, 84.4) * mm});
            skLineSegment(sketch, "E32.0.7.22", {"start": v(-10, 87) * mm, "end": v(-10, 87.4) * mm});
            skLineSegment(sketch, "E32.0.7.23", {"start": v(-12, 89) * mm, "end": v(-12, 89.4) * mm});
            skLineSegment(sketch, "E32.0.7.24", {"start": v(-10, 85) * mm, "end": v(-10, 85.4) * mm});
            skLineSegment(sketch, "E32.0.7.25", {"start": v(-12, 84) * mm, "end": v(-12, 84.4) * mm});
            skLineSegment(sketch, "E32.0.7.26", {"start": v(-12, 86) * mm, "end": v(-12, 86.4) * mm});
            skLineSegment(sketch, "E32.0.7.27", {"start": v(-10, 88) * mm, "end": v(-10, 88.4) * mm});
            skLineSegment(sketch, "E32.0.7.28", {"start": v(-12, 88) * mm, "end": v(-12, 88.4) * mm});
            skLineSegment(sketch, "E32.0.7.29", {"start": v(-10, 81) * mm, "end": v(-10, 81.4) * mm});
            skLineSegment(sketch, "E32.0.7.30", {"start": v(-10, 86) * mm, "end": v(-10, 86.4) * mm});
            skLineSegment(sketch, "E32.0.7.31", {"start": v(-10, 89) * mm, "end": v(-10, 89.4) * mm});
            skLineSegment(sketch, "E32.0.7.32", {"start": v(-12, 82) * mm, "end": v(-12, 82.4) * mm});
            skLineSegment(sketch, "E32.0.7.33", {"start": v(-10, 83) * mm, "end": v(-10, 83.4) * mm});
            skLineSegment(sketch, "E32.0.7.34", {"start": v(-13, 85) * mm, "end": v(-13, 85.4) * mm});
            skLineSegment(sketch, "E32.0.7.35", {"start": v(-10, 82) * mm, "end": v(-10, 82.4) * mm});
            skLineSegment(sketch, "E32.0.7.36", {"start": v(-12, 87) * mm, "end": v(-12, 87.4) * mm});
            skLineSegment(sketch, "E32.0.7.37", {"start": v(-12, 83) * mm, "end": v(-12, 83.4) * mm});
            skLineSegment(sketch, "E32.0.8.0", {"start": v(-12, 92) * mm, "end": v(-10, 92) * mm});
            skLineSegment(sketch, "E32.0.8.1", {"start": v(-12, 91.4) * mm, "end": v(-10, 91.4) * mm});
            skLineSegment(sketch, "E32.0.8.2", {"start": v(-12, 93.4) * mm, "end": v(-10, 93.4) * mm});
            skLineSegment(sketch, "E32.0.8.3", {"start": v(-12, 98.4) * mm, "end": v(-10, 98.4) * mm});
            skLineSegment(sketch, "E32.0.8.4", {"start": v(-12, 92.4) * mm, "end": v(-10, 92.4) * mm});
            skLineSegment(sketch, "E32.0.8.5", {"start": v(-12, 93) * mm, "end": v(-10, 93) * mm});
            skLineSegment(sketch, "E32.0.8.6", {"start": v(-10, 95.4) * mm, "end": v(-13, 95.4) * mm});
            skLineSegment(sketch, "E32.0.8.7", {"start": v(-12, 99) * mm, "end": v(-10, 99) * mm});
            skLineSegment(sketch, "E32.0.8.8", {"start": v(-12, 99.4) * mm, "end": v(-10, 99.4) * mm});
            skLineSegment(sketch, "E32.0.8.9", {"start": v(-12, 94.4) * mm, "end": v(-10, 94.4) * mm});
            skLineSegment(sketch, "E32.0.8.10", {"start": v(-12, 98) * mm, "end": v(-10, 98) * mm});
            skLineSegment(sketch, "E32.0.8.11", {"start": v(-12, 96) * mm, "end": v(-10, 96) * mm});
            skLineSegment(sketch, "E32.0.8.12", {"start": v(-12, 97) * mm, "end": v(-10, 97) * mm});
            skLineSegment(sketch, "E32.0.8.13", {"start": v(-12, 96.4) * mm, "end": v(-10, 96.4) * mm});
            skLineSegment(sketch, "E32.0.8.14", {"start": v(-12, 91) * mm, "end": v(-10, 91) * mm});
            skLineSegment(sketch, "E32.0.8.15", {"start": v(-10, 95) * mm, "end": v(-13, 95) * mm});
            skLineSegment(sketch, "E32.0.8.16", {"start": v(-12, 80) * mm, "end": v(-12, 230) * mm, "construction": true});
            skLineSegment(sketch, "E32.0.8.17", {"start": v(-13, 80) * mm, "end": v(-13, 230) * mm, "construction": true});
            skLineSegment(sketch, "E32.0.8.18", {"start": v(-12, 94) * mm, "end": v(-10, 94) * mm});
            skLineSegment(sketch, "E32.0.8.19", {"start": v(-12, 97.4) * mm, "end": v(-10, 97.4) * mm});
            skLineSegment(sketch, "E32.0.8.20", {"start": v(-12, 91) * mm, "end": v(-12, 91.4) * mm});
            skLineSegment(sketch, "E32.0.8.21", {"start": v(-10, 94) * mm, "end": v(-10, 94.4) * mm});
            skLineSegment(sketch, "E32.0.8.22", {"start": v(-10, 97) * mm, "end": v(-10, 97.4) * mm});
            skLineSegment(sketch, "E32.0.8.23", {"start": v(-12, 99) * mm, "end": v(-12, 99.4) * mm});
            skLineSegment(sketch, "E32.0.8.24", {"start": v(-10, 95) * mm, "end": v(-10, 95.4) * mm});
            skLineSegment(sketch, "E32.0.8.25", {"start": v(-12, 94) * mm, "end": v(-12, 94.4) * mm});
            skLineSegment(sketch, "E32.0.8.26", {"start": v(-12, 96) * mm, "end": v(-12, 96.4) * mm});
            skLineSegment(sketch, "E32.0.8.27", {"start": v(-10, 98) * mm, "end": v(-10, 98.4) * mm});
            skLineSegment(sketch, "E32.0.8.28", {"start": v(-12, 98) * mm, "end": v(-12, 98.4) * mm});
            skLineSegment(sketch, "E32.0.8.29", {"start": v(-10, 91) * mm, "end": v(-10, 91.4) * mm});
            skLineSegment(sketch, "E32.0.8.30", {"start": v(-10, 96) * mm, "end": v(-10, 96.4) * mm});
            skLineSegment(sketch, "E32.0.8.31", {"start": v(-10, 99) * mm, "end": v(-10, 99.4) * mm});
            skLineSegment(sketch, "E32.0.8.32", {"start": v(-12, 92) * mm, "end": v(-12, 92.4) * mm});
            skLineSegment(sketch, "E32.0.8.33", {"start": v(-10, 93) * mm, "end": v(-10, 93.4) * mm});
            skLineSegment(sketch, "E32.0.8.34", {"start": v(-13, 95) * mm, "end": v(-13, 95.4) * mm});
            skLineSegment(sketch, "E32.0.8.35", {"start": v(-10, 92) * mm, "end": v(-10, 92.4) * mm});
            skLineSegment(sketch, "E32.0.8.36", {"start": v(-12, 97) * mm, "end": v(-12, 97.4) * mm});
            skLineSegment(sketch, "E32.0.8.37", {"start": v(-12, 93) * mm, "end": v(-12, 93.4) * mm});
            skLineSegment(sketch, "E32.0.9.0", {"start": v(-12, 102) * mm, "end": v(-10, 102) * mm});
            skLineSegment(sketch, "E32.0.9.1", {"start": v(-12, 101.4) * mm, "end": v(-10, 101.4) * mm});
            skLineSegment(sketch, "E32.0.9.2", {"start": v(-12, 103.4) * mm, "end": v(-10, 103.4) * mm});
            skLineSegment(sketch, "E32.0.9.3", {"start": v(-12, 108.4) * mm, "end": v(-10, 108.4) * mm});
            skLineSegment(sketch, "E32.0.9.4", {"start": v(-12, 102.4) * mm, "end": v(-10, 102.4) * mm});
            skLineSegment(sketch, "E32.0.9.5", {"start": v(-12, 103) * mm, "end": v(-10, 103) * mm});
            skLineSegment(sketch, "E32.0.9.6", {"start": v(-10, 105.4) * mm, "end": v(-13, 105.4) * mm});
            skLineSegment(sketch, "E32.0.9.7", {"start": v(-12, 109) * mm, "end": v(-10, 109) * mm});
            skLineSegment(sketch, "E32.0.9.8", {"start": v(-12, 109.4) * mm, "end": v(-10, 109.4) * mm});
            skLineSegment(sketch, "E32.0.9.9", {"start": v(-12, 104.4) * mm, "end": v(-10, 104.4) * mm});
            skLineSegment(sketch, "E32.0.9.10", {"start": v(-12, 108) * mm, "end": v(-10, 108) * mm});
            skLineSegment(sketch, "E32.0.9.11", {"start": v(-12, 106) * mm, "end": v(-10, 106) * mm});
            skLineSegment(sketch, "E32.0.9.12", {"start": v(-12, 107) * mm, "end": v(-10, 107) * mm});
            skLineSegment(sketch, "E32.0.9.13", {"start": v(-12, 106.4) * mm, "end": v(-10, 106.4) * mm});
            skLineSegment(sketch, "E32.0.9.14", {"start": v(-12, 101) * mm, "end": v(-10, 101) * mm});
            skLineSegment(sketch, "E32.0.9.15", {"start": v(-10, 105) * mm, "end": v(-13, 105) * mm});
            skLineSegment(sketch, "E32.0.9.16", {"start": v(-12, 90) * mm, "end": v(-12, 240) * mm, "construction": true});
            skLineSegment(sketch, "E32.0.9.17", {"start": v(-13, 90) * mm, "end": v(-13, 240) * mm, "construction": true});
            skLineSegment(sketch, "E32.0.9.18", {"start": v(-12, 104) * mm, "end": v(-10, 104) * mm});
            skLineSegment(sketch, "E32.0.9.19", {"start": v(-12, 107.4) * mm, "end": v(-10, 107.4) * mm});
            skLineSegment(sketch, "E32.0.9.20", {"start": v(-12, 101) * mm, "end": v(-12, 101.4) * mm});
            skLineSegment(sketch, "E32.0.9.21", {"start": v(-10, 104) * mm, "end": v(-10, 104.4) * mm});
            skLineSegment(sketch, "E32.0.9.22", {"start": v(-10, 107) * mm, "end": v(-10, 107.4) * mm});
            skLineSegment(sketch, "E32.0.9.23", {"start": v(-12, 109) * mm, "end": v(-12, 109.4) * mm});
            skLineSegment(sketch, "E32.0.9.24", {"start": v(-10, 105) * mm, "end": v(-10, 105.4) * mm});
            skLineSegment(sketch, "E32.0.9.25", {"start": v(-12, 104) * mm, "end": v(-12, 104.4) * mm});
            skLineSegment(sketch, "E32.0.9.26", {"start": v(-12, 106) * mm, "end": v(-12, 106.4) * mm});
            skLineSegment(sketch, "E32.0.9.27", {"start": v(-10, 108) * mm, "end": v(-10, 108.4) * mm});
            skLineSegment(sketch, "E32.0.9.28", {"start": v(-12, 108) * mm, "end": v(-12, 108.4) * mm});
            skLineSegment(sketch, "E32.0.9.29", {"start": v(-10, 101) * mm, "end": v(-10, 101.4) * mm});
            skLineSegment(sketch, "E32.0.9.30", {"start": v(-10, 106) * mm, "end": v(-10, 106.4) * mm});
            skLineSegment(sketch, "E32.0.9.31", {"start": v(-10, 109) * mm, "end": v(-10, 109.4) * mm});
            skLineSegment(sketch, "E32.0.9.32", {"start": v(-12, 102) * mm, "end": v(-12, 102.4) * mm});
            skLineSegment(sketch, "E32.0.9.33", {"start": v(-10, 103) * mm, "end": v(-10, 103.4) * mm});
            skLineSegment(sketch, "E32.0.9.34", {"start": v(-13, 105) * mm, "end": v(-13, 105.4) * mm});
            skLineSegment(sketch, "E32.0.9.35", {"start": v(-10, 102) * mm, "end": v(-10, 102.4) * mm});
            skLineSegment(sketch, "E32.0.9.36", {"start": v(-12, 107) * mm, "end": v(-12, 107.4) * mm});
            skLineSegment(sketch, "E32.0.9.37", {"start": v(-12, 103) * mm, "end": v(-12, 103.4) * mm});
            skLineSegment(sketch, "E32.0.10.0", {"start": v(-12, 112) * mm, "end": v(-10, 112) * mm});
            skLineSegment(sketch, "E32.0.10.1", {"start": v(-12, 111.4) * mm, "end": v(-10, 111.4) * mm});
            skLineSegment(sketch, "E32.0.10.2", {"start": v(-12, 113.4) * mm, "end": v(-10, 113.4) * mm});
            skLineSegment(sketch, "E32.0.10.3", {"start": v(-12, 118.4) * mm, "end": v(-10, 118.4) * mm});
            skLineSegment(sketch, "E32.0.10.4", {"start": v(-12, 112.4) * mm, "end": v(-10, 112.4) * mm});
            skLineSegment(sketch, "E32.0.10.5", {"start": v(-12, 113) * mm, "end": v(-10, 113) * mm});
            skLineSegment(sketch, "E32.0.10.6", {"start": v(-10, 115.4) * mm, "end": v(-13, 115.4) * mm});
            skLineSegment(sketch, "E32.0.10.7", {"start": v(-12, 119) * mm, "end": v(-10, 119) * mm});
            skLineSegment(sketch, "E32.0.10.8", {"start": v(-12, 119.4) * mm, "end": v(-10, 119.4) * mm});
            skLineSegment(sketch, "E32.0.10.9", {"start": v(-12, 114.4) * mm, "end": v(-10, 114.4) * mm});
            skLineSegment(sketch, "E32.0.10.10", {"start": v(-12, 118) * mm, "end": v(-10, 118) * mm});
            skLineSegment(sketch, "E32.0.10.11", {"start": v(-12, 116) * mm, "end": v(-10, 116) * mm});
            skLineSegment(sketch, "E32.0.10.12", {"start": v(-12, 117) * mm, "end": v(-10, 117) * mm});
            skLineSegment(sketch, "E32.0.10.13", {"start": v(-12, 116.4) * mm, "end": v(-10, 116.4) * mm});
            skLineSegment(sketch, "E32.0.10.14", {"start": v(-12, 111) * mm, "end": v(-10, 111) * mm});
            skLineSegment(sketch, "E32.0.10.15", {"start": v(-10, 115) * mm, "end": v(-13, 115) * mm});
            skLineSegment(sketch, "E32.0.10.16", {"start": v(-12, 100) * mm, "end": v(-12, 250) * mm, "construction": true});
            skLineSegment(sketch, "E32.0.10.17", {"start": v(-13, 100) * mm, "end": v(-13, 250) * mm, "construction": true});
            skLineSegment(sketch, "E32.0.10.18", {"start": v(-12, 114) * mm, "end": v(-10, 114) * mm});
            skLineSegment(sketch, "E32.0.10.19", {"start": v(-12, 117.4) * mm, "end": v(-10, 117.4) * mm});
            skLineSegment(sketch, "E32.0.10.20", {"start": v(-12, 111) * mm, "end": v(-12, 111.4) * mm});
            skLineSegment(sketch, "E32.0.10.21", {"start": v(-10, 114) * mm, "end": v(-10, 114.4) * mm});
            skLineSegment(sketch, "E32.0.10.22", {"start": v(-10, 117) * mm, "end": v(-10, 117.4) * mm});
            skLineSegment(sketch, "E32.0.10.23", {"start": v(-12, 119) * mm, "end": v(-12, 119.4) * mm});
            skLineSegment(sketch, "E32.0.10.24", {"start": v(-10, 115) * mm, "end": v(-10, 115.4) * mm});
            skLineSegment(sketch, "E32.0.10.25", {"start": v(-12, 114) * mm, "end": v(-12, 114.4) * mm});
            skLineSegment(sketch, "E32.0.10.26", {"start": v(-12, 116) * mm, "end": v(-12, 116.4) * mm});
            skLineSegment(sketch, "E32.0.10.27", {"start": v(-10, 118) * mm, "end": v(-10, 118.4) * mm});
            skLineSegment(sketch, "E32.0.10.28", {"start": v(-12, 118) * mm, "end": v(-12, 118.4) * mm});
            skLineSegment(sketch, "E32.0.10.29", {"start": v(-10, 111) * mm, "end": v(-10, 111.4) * mm});
            skLineSegment(sketch, "E32.0.10.30", {"start": v(-10, 116) * mm, "end": v(-10, 116.4) * mm});
            skLineSegment(sketch, "E32.0.10.31", {"start": v(-10, 119) * mm, "end": v(-10, 119.4) * mm});
            skLineSegment(sketch, "E32.0.10.32", {"start": v(-12, 112) * mm, "end": v(-12, 112.4) * mm});
            skLineSegment(sketch, "E32.0.10.33", {"start": v(-10, 113) * mm, "end": v(-10, 113.4) * mm});
            skLineSegment(sketch, "E32.0.10.34", {"start": v(-13, 115) * mm, "end": v(-13, 115.4) * mm});
            skLineSegment(sketch, "E32.0.10.35", {"start": v(-10, 112) * mm, "end": v(-10, 112.4) * mm});
            skLineSegment(sketch, "E32.0.10.36", {"start": v(-12, 117) * mm, "end": v(-12, 117.4) * mm});
            skLineSegment(sketch, "E32.0.10.37", {"start": v(-12, 113) * mm, "end": v(-12, 113.4) * mm});
            skLineSegment(sketch, "E32.0.11.0", {"start": v(-12, 122) * mm, "end": v(-10, 122) * mm});
            skLineSegment(sketch, "E32.0.11.1", {"start": v(-12, 121.4) * mm, "end": v(-10, 121.4) * mm});
            skLineSegment(sketch, "E32.0.11.2", {"start": v(-12, 123.4) * mm, "end": v(-10, 123.4) * mm});
            skLineSegment(sketch, "E32.0.11.3", {"start": v(-12, 128.4) * mm, "end": v(-10, 128.4) * mm});
            skLineSegment(sketch, "E32.0.11.4", {"start": v(-12, 122.4) * mm, "end": v(-10, 122.4) * mm});
            skLineSegment(sketch, "E32.0.11.5", {"start": v(-12, 123) * mm, "end": v(-10, 123) * mm});
            skLineSegment(sketch, "E32.0.11.6", {"start": v(-10, 125.4) * mm, "end": v(-13, 125.4) * mm});
            skLineSegment(sketch, "E32.0.11.7", {"start": v(-12, 129) * mm, "end": v(-10, 129) * mm});
            skLineSegment(sketch, "E32.0.11.8", {"start": v(-12, 129.4) * mm, "end": v(-10, 129.4) * mm});
            skLineSegment(sketch, "E32.0.11.9", {"start": v(-12, 124.4) * mm, "end": v(-10, 124.4) * mm});
            skLineSegment(sketch, "E32.0.11.10", {"start": v(-12, 128) * mm, "end": v(-10, 128) * mm});
            skLineSegment(sketch, "E32.0.11.11", {"start": v(-12, 126) * mm, "end": v(-10, 126) * mm});
            skLineSegment(sketch, "E32.0.11.12", {"start": v(-12, 127) * mm, "end": v(-10, 127) * mm});
            skLineSegment(sketch, "E32.0.11.13", {"start": v(-12, 126.4) * mm, "end": v(-10, 126.4) * mm});
            skLineSegment(sketch, "E32.0.11.14", {"start": v(-12, 121) * mm, "end": v(-10, 121) * mm});
            skLineSegment(sketch, "E32.0.11.15", {"start": v(-10, 125) * mm, "end": v(-13, 125) * mm});
            skLineSegment(sketch, "E32.0.11.16", {"start": v(-12, 110) * mm, "end": v(-12, 260) * mm, "construction": true});
            skLineSegment(sketch, "E32.0.11.17", {"start": v(-13, 110) * mm, "end": v(-13, 260) * mm, "construction": true});
            skLineSegment(sketch, "E32.0.11.18", {"start": v(-12, 124) * mm, "end": v(-10, 124) * mm});
            skLineSegment(sketch, "E32.0.11.19", {"start": v(-12, 127.4) * mm, "end": v(-10, 127.4) * mm});
            skLineSegment(sketch, "E32.0.11.20", {"start": v(-12, 121) * mm, "end": v(-12, 121.4) * mm});
            skLineSegment(sketch, "E32.0.11.21", {"start": v(-10, 124) * mm, "end": v(-10, 124.4) * mm});
            skLineSegment(sketch, "E32.0.11.22", {"start": v(-10, 127) * mm, "end": v(-10, 127.4) * mm});
            skLineSegment(sketch, "E32.0.11.23", {"start": v(-12, 129) * mm, "end": v(-12, 129.4) * mm});
            skLineSegment(sketch, "E32.0.11.24", {"start": v(-10, 125) * mm, "end": v(-10, 125.4) * mm});
            skLineSegment(sketch, "E32.0.11.25", {"start": v(-12, 124) * mm, "end": v(-12, 124.4) * mm});
            skLineSegment(sketch, "E32.0.11.26", {"start": v(-12, 126) * mm, "end": v(-12, 126.4) * mm});
            skLineSegment(sketch, "E32.0.11.27", {"start": v(-10, 128) * mm, "end": v(-10, 128.4) * mm});
            skLineSegment(sketch, "E32.0.11.28", {"start": v(-12, 128) * mm, "end": v(-12, 128.4) * mm});
            skLineSegment(sketch, "E32.0.11.29", {"start": v(-10, 121) * mm, "end": v(-10, 121.4) * mm});
            skLineSegment(sketch, "E32.0.11.30", {"start": v(-10, 126) * mm, "end": v(-10, 126.4) * mm});
            skLineSegment(sketch, "E32.0.11.31", {"start": v(-10, 129) * mm, "end": v(-10, 129.4) * mm});
            skLineSegment(sketch, "E32.0.11.32", {"start": v(-12, 122) * mm, "end": v(-12, 122.4) * mm});
            skLineSegment(sketch, "E32.0.11.33", {"start": v(-10, 123) * mm, "end": v(-10, 123.4) * mm});
            skLineSegment(sketch, "E32.0.11.34", {"start": v(-13, 125) * mm, "end": v(-13, 125.4) * mm});
            skLineSegment(sketch, "E32.0.11.35", {"start": v(-10, 122) * mm, "end": v(-10, 122.4) * mm});
            skLineSegment(sketch, "E32.0.11.36", {"start": v(-12, 127) * mm, "end": v(-12, 127.4) * mm});
            skLineSegment(sketch, "E32.0.11.37", {"start": v(-12, 123) * mm, "end": v(-12, 123.4) * mm});
            skLineSegment(sketch, "E32.0.12.0", {"start": v(-12, 132) * mm, "end": v(-10, 132) * mm});
            skLineSegment(sketch, "E32.0.12.1", {"start": v(-12, 131.4) * mm, "end": v(-10, 131.4) * mm});
            skLineSegment(sketch, "E32.0.12.2", {"start": v(-12, 133.4) * mm, "end": v(-10, 133.4) * mm});
            skLineSegment(sketch, "E32.0.12.3", {"start": v(-12, 138.4) * mm, "end": v(-10, 138.4) * mm});
            skLineSegment(sketch, "E32.0.12.4", {"start": v(-12, 132.4) * mm, "end": v(-10, 132.4) * mm});
            skLineSegment(sketch, "E32.0.12.5", {"start": v(-12, 133) * mm, "end": v(-10, 133) * mm});
            skLineSegment(sketch, "E32.0.12.6", {"start": v(-10, 135.4) * mm, "end": v(-13, 135.4) * mm});
            skLineSegment(sketch, "E32.0.12.7", {"start": v(-12, 139) * mm, "end": v(-10, 139) * mm});
            skLineSegment(sketch, "E32.0.12.8", {"start": v(-12, 139.4) * mm, "end": v(-10, 139.4) * mm});
            skLineSegment(sketch, "E32.0.12.9", {"start": v(-12, 134.4) * mm, "end": v(-10, 134.4) * mm});
            skLineSegment(sketch, "E32.0.12.10", {"start": v(-12, 138) * mm, "end": v(-10, 138) * mm});
            skLineSegment(sketch, "E32.0.12.11", {"start": v(-12, 136) * mm, "end": v(-10, 136) * mm});
            skLineSegment(sketch, "E32.0.12.12", {"start": v(-12, 137) * mm, "end": v(-10, 137) * mm});
            skLineSegment(sketch, "E32.0.12.13", {"start": v(-12, 136.4) * mm, "end": v(-10, 136.4) * mm});
            skLineSegment(sketch, "E32.0.12.14", {"start": v(-12, 131) * mm, "end": v(-10, 131) * mm});
            skLineSegment(sketch, "E32.0.12.15", {"start": v(-10, 135) * mm, "end": v(-13, 135) * mm});
            skLineSegment(sketch, "E32.0.12.16", {"start": v(-12, 120) * mm, "end": v(-12, 270) * mm, "construction": true});
            skLineSegment(sketch, "E32.0.12.17", {"start": v(-13, 120) * mm, "end": v(-13, 270) * mm, "construction": true});
            skLineSegment(sketch, "E32.0.12.18", {"start": v(-12, 134) * mm, "end": v(-10, 134) * mm});
            skLineSegment(sketch, "E32.0.12.19", {"start": v(-12, 137.4) * mm, "end": v(-10, 137.4) * mm});
            skLineSegment(sketch, "E32.0.12.20", {"start": v(-12, 131) * mm, "end": v(-12, 131.4) * mm});
            skLineSegment(sketch, "E32.0.12.21", {"start": v(-10, 134) * mm, "end": v(-10, 134.4) * mm});
            skLineSegment(sketch, "E32.0.12.22", {"start": v(-10, 137) * mm, "end": v(-10, 137.4) * mm});
            skLineSegment(sketch, "E32.0.12.23", {"start": v(-12, 139) * mm, "end": v(-12, 139.4) * mm});
            skLineSegment(sketch, "E32.0.12.24", {"start": v(-10, 135) * mm, "end": v(-10, 135.4) * mm});
            skLineSegment(sketch, "E32.0.12.25", {"start": v(-12, 134) * mm, "end": v(-12, 134.4) * mm});
            skLineSegment(sketch, "E32.0.12.26", {"start": v(-12, 136) * mm, "end": v(-12, 136.4) * mm});
            skLineSegment(sketch, "E32.0.12.27", {"start": v(-10, 138) * mm, "end": v(-10, 138.4) * mm});
            skLineSegment(sketch, "E32.0.12.28", {"start": v(-12, 138) * mm, "end": v(-12, 138.4) * mm});
            skLineSegment(sketch, "E32.0.12.29", {"start": v(-10, 131) * mm, "end": v(-10, 131.4) * mm});
            skLineSegment(sketch, "E32.0.12.30", {"start": v(-10, 136) * mm, "end": v(-10, 136.4) * mm});
            skLineSegment(sketch, "E32.0.12.31", {"start": v(-10, 139) * mm, "end": v(-10, 139.4) * mm});
            skLineSegment(sketch, "E32.0.12.32", {"start": v(-12, 132) * mm, "end": v(-12, 132.4) * mm});
            skLineSegment(sketch, "E32.0.12.33", {"start": v(-10, 133) * mm, "end": v(-10, 133.4) * mm});
            skLineSegment(sketch, "E32.0.12.34", {"start": v(-13, 135) * mm, "end": v(-13, 135.4) * mm});
            skLineSegment(sketch, "E32.0.12.35", {"start": v(-10, 132) * mm, "end": v(-10, 132.4) * mm});
            skLineSegment(sketch, "E32.0.12.36", {"start": v(-12, 137) * mm, "end": v(-12, 137.4) * mm});
            skLineSegment(sketch, "E32.0.12.37", {"start": v(-12, 133) * mm, "end": v(-12, 133.4) * mm});
            skLineSegment(sketch, "E32.direction1", {"start": v(-13, 0) * mm, "end": v(12, 0) * mm, "construction": true});
            skLineSegment(sketch, "E32.direction2", {"start": v(-13, 0) * mm, "end": v(-13, 10) * mm, "construction": true});
            const initialGuessF2  = {"E10": [-0.017, 0.01082, 0, -1, 0.002], "E11": [-0.015, 0.01943, 0, 1, 0.002], "E12": [-0.015, 0.0292, 0, 1, 0.002], "E13": [-0.015, 0.0392, 0, 1, 0.002], "E14": [-0.015, 0.04914, 0, 1, 0.002], "E15": [-0.015, 0.0592, 0, 1, 0.002], "E16": [-0.015, 0.069, 0, 1, 0.00247], "E17": [-0.015, 0.079, 0, 1, 0.00247], "E18": [-0.015, 0.089, 0, 1, 0.00247], "E19": [-0.015, 0.099, 0, 1, 0.00247], "E20": [-0.015, 0.10821, 0, 1, 0.00222], "E21": [-0.015, 0.11848, 0, 1, 0.00222], "E22": [-0.015, 0.12822, 0, 1, 0.00222], "E23": [-0.015, 0.13823, 0, 1, 0.00222]};
            skSetInitialGuess(sketch, initialGuessF2);
            skSolve(sketch);
        }
        {
            var Q0;
            Q0=qSketchRegion(id+"F2",true);
            extrude(context, id + "F3", {"entities" : qUnion([Q0]), "operationType" : NewBodyOperationType.ADD, "endBound" : BoundingType.SYMMETRIC, "oppositeDirection" : true, "depth" : 10 * mm, "offsetDistance" : 25 * mm});
        }
        {
            var Q0;
            Q0=qCreatedBy(makeId("Right.planeOp"),FACE);
            var sketch = newSketch(context, id + "F4", { "sketchPlane" : qUnion([Q0])});
            skLineSegment(sketch, "E33.bottom", {"start": v(26.29, 33.53) * mm, "end": v(34.29, 33.53) * mm});
            skLineSegment(sketch, "E33.top", {"start": v(26.29, 158.53) * mm, "end": v(34.29, 158.53) * mm});
            skLineSegment(sketch, "E33.left", {"start": v(26.29, 33.53) * mm, "end": v(26.29, 158.53) * mm});
            skLineSegment(sketch, "E33.right", {"start": v(34.29, 33.53) * mm, "end": v(34.29, 158.53) * mm});
            skSolve(sketch);
        }
        {
            var Q0;
            Q0=qSketchRegion(id+"F4",true);
            extrude(context, id + "F5", {"entities" : qUnion([Q0]), "depth" : 0.5 * mm, "offsetDistance" : 25 * mm});
        }
        {
            var Q0;
            Q0=makeQuery(id+"F5.opExtrude","SWEPT_EDGE",EDGE,{"disambiguationData":[OSD([sQuery(id+"F4.wireOp",EDGE,"E33.top"),sQuery(id+"F4.wireOp",EDGE,"E33.left")])]});
            var Q1;
            Q1=makeQuery(id+"F5.opExtrude","SWEPT_EDGE",EDGE,{"disambiguationData":[OSD([sQuery(id+"F4.wireOp",EDGE,"E33.top"),sQuery(id+"F4.wireOp",EDGE,"E33.right")])]});
            var Q2;
            Q2=makeQuery(id+"F5.opExtrude","SWEPT_EDGE",EDGE,{"disambiguationData":[OSD([sQuery(id+"F4.wireOp",EDGE,"E33.bottom"),sQuery(id+"F4.wireOp",EDGE,"E33.right")])]});
            var Q3;
            Q3=makeQuery(id+"F5.opExtrude","SWEPT_EDGE",EDGE,{"disambiguationData":[OSD([sQuery(id+"F4.wireOp",EDGE,"E33.bottom"),sQuery(id+"F4.wireOp",EDGE,"E33.left")])]});
            fillet(context, id + "F6", {"entities" : qUnion([Q0, Q1, Q2, Q3]), "radius" : 2 * mm, "tangentPropagation" : true, "allowEdgeOverflow" : false});
        }
        {
            var Q0;
            Q0=makeQuery(id+"F5.opExtrude","CAP_FACE",FACE,{"disambiguationData":[OSD([sQuery(id+"F4.wireOp",EDGE,"E33.bottom"),sQuery(id+"F4.wireOp",EDGE,"E33.top"),sQuery(id+"F4.wireOp",EDGE,"E33.left"),sQuery(id+"F4.wireOp",EDGE,"E33.right")])],"isStart":false});
            var sketch = newSketch(context, id + "F7", { "sketchPlane" : qUnion([Q0])});
            skLineSegment(sketch, "E34", {"start": v(26.29, 135.36) * mm, "end": v(34.29, 135.36) * mm, "construction": true});
            skLineSegment(sketch, "E35", {"start": v(30.29, 152.58) * mm, "end": v(30.29, 95.45) * mm, "construction": true});
            skPoint(sketch, "E36", {"position": v(30.29, 135.36) * mm});
            skLineSegment(sketch, "E37.top", {"start": v(28.46, 115.03) * mm, "end": v(32.12, 115.03) * mm});
            skLineSegment(sketch, "E37.left", {"start": v(28.46, 133.53) * mm, "end": v(28.46, 115.03) * mm});
            skLineSegment(sketch, "E37.right", {"start": v(32.12, 133.53) * mm, "end": v(32.12, 115.03) * mm});
            skPoint(sketch, "E37.middle", {"position": v(30.29, 124.28) * mm});
            skArc(sketch, "E38", {"start": v(32.12, 133.53) * mm, "mid": v(30.29, 135.36) * mm, "end": v(28.46, 133.53) * mm});
            skLineSegment(sketch, "E39", {"start": v(34.29, 79.03) * mm, "end": v(26.29, 79.03) * mm, "construction": true});
            skCircle(sketch, "E40", {"center": v(30.29, 79.03) * mm, "radius": 1 * mm});
            skSolve(sketch);
        }
        {
            var Q0;
            Q0=qSketchRegion(id+"F7",true);
            extrude(context, id + "F8", {"entities" : qUnion([Q0]), "operationType" : NewBodyOperationType.REMOVE, "endBound" : BoundingType.SYMMETRIC, "oppositeDirection" : true, "depth" : 25 * mm, "offsetDistance" : 25 * mm});
        }
        {
            var Q0;
            Q0=makeQuery(id+"F5.opExtrude","CAP_EDGE",EDGE,{"disambiguationData":[OSD([sQuery(id+"F4.wireOp",EDGE,"E33.right")])],"isStart":false});
            chamfer(context, id + "F9", {"entities" : qUnion([Q0]), "chamferType" : ChamferType.OFFSET_ANGLE, "width" : 0.5 * mm, "oppositeDirection" : false, "angle" : 45 * degree});
        }
        {
            var Q0;
            Q0=makeQuery(id+"F1.opExtrude","SWEPT_BODY",BODY,{"disambiguationData":[OSD([sQuery(id+"F0.wireOp",EDGE,"E0.bottom"),sQuery(id+"F0.wireOp",EDGE,"E0.top"),sQuery(id+"F0.wireOp",EDGE,"E0.left"),sQuery(id+"F0.wireOp",EDGE,"E0.right")])]});
            transform(context, id + "F10", {"entities" : qUnion([Q0]), "transformType" : TransformType.TRANSLATION_3D, "dx" : 5.3 * mm, "dy" : 45 * mm, "dz" : 25 * mm, "makeCopy" : false});
        }
        {
            var Q0;
            {var subQ0=sQuery(id+"F0.wireOp",EDGE,"E0.top");var subQ1=sQuery(id+"F0.wireOp",EDGE,"E0.right");var subQ2=sQuery(id+"F0.wireOp",EDGE,"E0.bottom");var subQ3=sQuery(id+"F0.wireOp",EDGE,"E0.left");Q0=makeQuery(id+"F3.boolean.opBoolean","SPLIT",FACE,{"disambiguationData":[TD([makeQuery(id+"F1.opExtrude","SWEPT_FACE",FACE,{"disambiguationData":[OSD([subQ2])]})])],"derivedFrom":makeQuery(id+"F1.opExtrude","CAP_FACE",FACE,{"disambiguationData":[OSD([subQ2,subQ0,subQ3,subQ1])],"isStart":false})});}
            var sketch = newSketch(context, id + "F11", { "sketchPlane" : qUnion([Q0])});
            skLineSegment(sketch, "E41.bottom", {"start": v(6.31, 193.14) * mm, "end": v(49.94, 193.14) * mm});
            skLineSegment(sketch, "E41.top", {"start": v(6.31, 157.78) * mm, "end": v(49.94, 157.78) * mm});
            skLineSegment(sketch, "E41.left", {"start": v(6.31, 193.14) * mm, "end": v(6.31, 157.78) * mm});
            skLineSegment(sketch, "E41.right", {"start": v(49.94, 193.14) * mm, "end": v(49.94, 157.78) * mm});
            skLineSegment(sketch, "E42.bottom", {"start": v(54.17, 196.62) * mm, "end": v(32, 196.62) * mm});
            skLineSegment(sketch, "E42.top", {"start": v(54.17, 155.9) * mm, "end": v(32, 155.9) * mm});
            skLineSegment(sketch, "E42.left", {"start": v(54.17, 196.62) * mm, "end": v(54.17, 155.9) * mm});
            skLineSegment(sketch, "E42.right", {"start": v(32, 196.62) * mm, "end": v(32, 155.9) * mm});
            skSolve(sketch);
        }
        {
            var Q0;
            Q0=qSketchRegion(id+"F11",true);
            extrude(context, id + "F12", {"entities" : qUnion([Q0]), "operationType" : NewBodyOperationType.REMOVE, "endBound" : BoundingType.SYMMETRIC, "oppositeDirection" : true, "depth" : 25 * mm, "offsetDistance" : 25 * mm});
        }
        {
            var Q0;
            Q0=makeQuery(id+"F1.opExtrude","SWEPT_BODY",BODY,{"disambiguationData":[OSD([sQuery(id+"F0.wireOp",EDGE,"E0.bottom"),sQuery(id+"F0.wireOp",EDGE,"E0.top"),sQuery(id+"F0.wireOp",EDGE,"E0.left"),sQuery(id+"F0.wireOp",EDGE,"E0.right")])]});
            var Q1;
            Q1=makeQuery(id+"F5.opExtrude","SWEPT_BODY",BODY,{"disambiguationData":[OSD([sQuery(id+"F4.wireOp",EDGE,"E33.bottom"),sQuery(id+"F4.wireOp",EDGE,"E33.top"),sQuery(id+"F4.wireOp",EDGE,"E33.left"),sQuery(id+"F4.wireOp",EDGE,"E33.right")])]});
            booleanBodies(context, id + "F13", {"operationType" : BooleanOperationType.SUBTRACTION, "tools" : qUnion([Q0]), "targets" : qUnion([Q1])});
        }
    });
